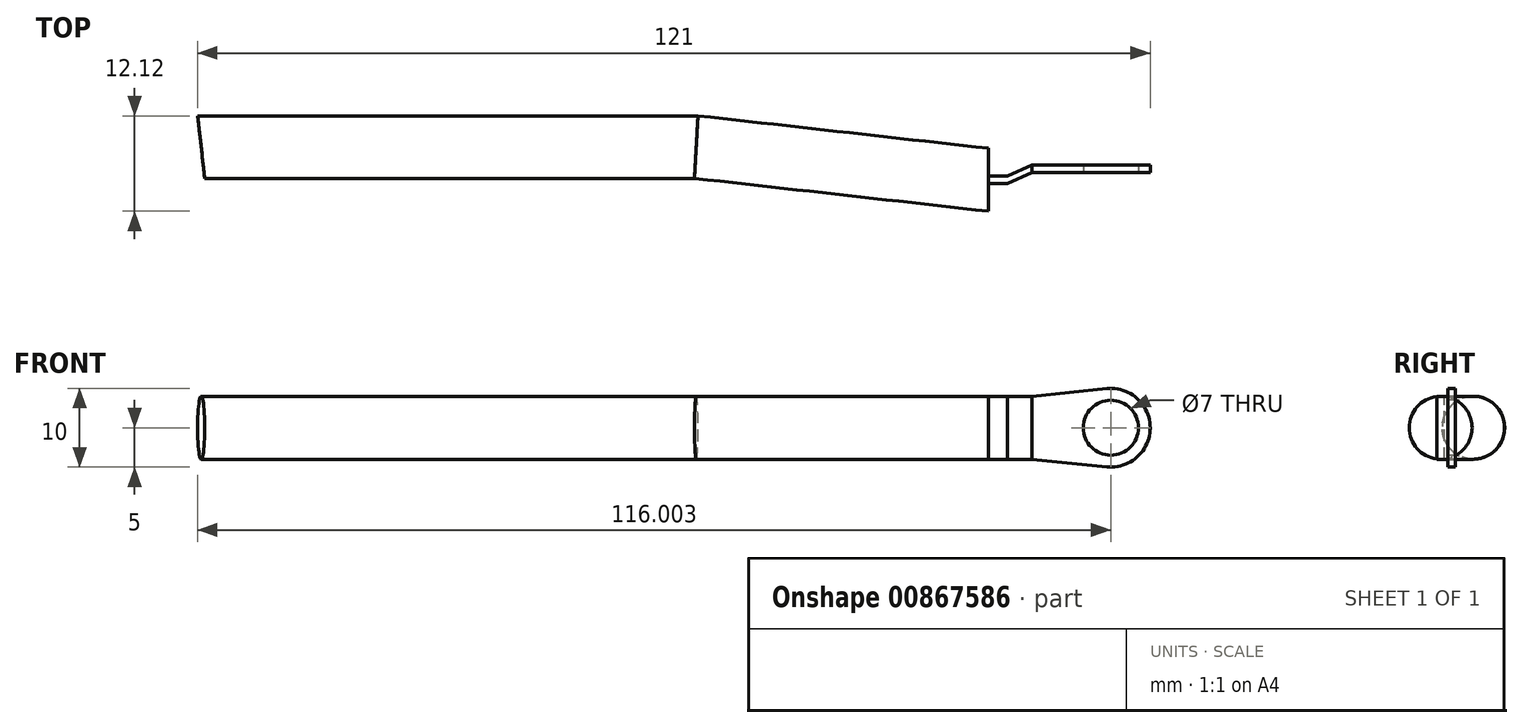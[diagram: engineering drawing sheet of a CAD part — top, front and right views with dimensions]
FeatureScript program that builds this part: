
annotation { "Feature Type Name" : "Feature", "Feature Type Description" : "" }
export const myFeature = defineFeature(function(context is Context, id is Id, definition is map)
    precondition{}
    {
        {
            var Q0;
            Q0=qCreatedBy(makeId("Front.planeOp"),FACE);
            var sketch = newSketch(context, id + "F0", { "sketchPlane" : qUnion([Q0])});
            skArc(sketch, "E0", {"start": v(12.63, -4.97) * mm, "mid": v(18.14, 0) * mm, "end": v(12.63, 4.97) * mm});
            skLineSegment(sketch, "E1", {"start": v(3.14, 4) * mm, "end": v(3.14, -4) * mm});
            skLineSegment(sketch, "E2", {"start": v(3.14, -4) * mm, "end": v(12.63, -4.97) * mm});
            skLineSegment(sketch, "E3", {"start": v(3.14, 4) * mm, "end": v(12.63, 4.97) * mm});
            skSolve(sketch);
        }
        {
            var Q0;
            Q0 = qSketchRegion(id + "F0", true);
            extrude(context, id + "F1", {"entities" : qUnion([Q0]), "endBound" : BoundingType.SYMMETRIC, "depth" : 1 * mm, "offsetDistance" : 25 * mm});
        }
        {
            var Q0;
            Q0=makeQuery(id+"F1.opExtrude","CAP_FACE",FACE,{"disambiguationData":[OSD([sQuery(id+"F0.wireOp",EDGE,"E0"),sQuery(id+"F0.wireOp",EDGE,"E1"),sQuery(id+"F0.wireOp",EDGE,"E2"),sQuery(id+"F0.wireOp",EDGE,"E3")])],"isStart":false});
            var sketch = newSketch(context, id + "F2", { "sketchPlane" : qUnion([Q0])});
            skCircle(sketch, "E4", {"center": v(13.14, 0) * mm, "radius": 3.5 * mm});
            skSolve(sketch);
        }
        {
            var Q0;
            Q0 = qSketchRegion(id + "F2", true);
            extrude(context, id + "F3", {"entities" : qUnion([Q0]), "operationType" : NewBodyOperationType.REMOVE, "oppositeDirection" : true, "depth" : 25 * mm, "offsetDistance" : 25 * mm});
        }
        {
            var Q0;
            Q0=qCreatedBy(makeId("Top.planeOp"),FACE);
            cPlane(context, id + "F4", {"entities" : qUnion([Q0]), "cplaneType" : CPlaneType.OFFSET, "offset" : 4 * mm, "flipAlignment" : true, "width" : 150 * mm, "height" : 150 * mm});
        }
        {
            var Q0;
            Q0=qCreatedBy(id+"F4.planeOp",FACE);
            var sketch = newSketch(context, id + "F5", { "sketchPlane" : qUnion([Q0])});
            skLineSegment(sketch, "E5", {"start": v(3.14, 0.5) * mm, "end": v(0, -0.9) * mm});
            skLineSegment(sketch, "E6", {"start": v(3.14, -0.5) * mm, "end": v(0, -1.9) * mm});
            skLineSegment(sketch, "E7", {"start": v(0, -0.9) * mm, "end": v(0, -1.9) * mm});
            skLineSegment(sketch, "E8", {"start": v(3.14, 0.5) * mm, "end": v(3.14, -0.5) * mm});
            skSolve(sketch);
        }
        {
            var Q0;
            Q0=qCreatedBy(id+"F4.planeOp",FACE);
            var sketch = newSketch(context, id + "F6", { "sketchPlane" : qUnion([Q0])});
            skLineSegment(sketch, "E9", {"start": v(0, -0.9) * mm, "end": v(-2.41, -0.9) * mm});
            skLineSegment(sketch, "E10", {"start": v(-2.41, -0.9) * mm, "end": v(-2.41, -1.9) * mm});
            skLineSegment(sketch, "E11", {"start": v(-2.41, -1.9) * mm, "end": v(0, -1.9) * mm});
            skLineSegment(sketch, "E12", {"start": v(0, -1.9) * mm, "end": v(0, -0.9) * mm});
            skSolve(sketch);
        }
        {
            var Q0;
            Q0 = qSketchRegion(id + "F5", true);
            var Q1;
            Q1 = qSketchRegion(id + "F6", true);
            extrude(context, id + "F7", {"entities" : qUnion([Q0, Q1]), "operationType" : NewBodyOperationType.ADD, "oppositeDirection" : true, "depth" : 8 * mm, "offsetDistance" : 25 * mm});
        }
        {
            var Q0;
            Q0=makeQuery(id+"F7.opExtrude","SWEPT_FACE",FACE,{"disambiguationData":[OSD([sQuery(id+"F6.wireOp",EDGE,"E10")])]});
            var sketch = newSketch(context, id + "F8", { "sketchPlane" : qUnion([Q0])});
            skCircle(sketch, "E13", {"center": v(1.4, 0) * mm, "radius": 4 * mm});
            skPoint(sketch, "E13.centerSnap0", {"position": v(1.9, 0) * mm});
            skPoint(sketch, "E13.centerSnap1", {"position": v(1.4, 4) * mm});
            skSolve(sketch);
        }
        {
            var Q0;
            {var subQ0=sQuery(id+"F8.wireOp",EDGE,"E13");var subQ1=sQuery(id+"F6.wireOp",EDGE,"E10");var subQ7=makeQuery(id+"F8.imprint","INTERSECT",VERTEX,{"derivedFrom":[makeQuery(id+"F7.opExtrude","CAP_EDGE",EDGE,{"disambiguationData":[OSD([subQ1])],"isStart":true}),subQ0]});Q0=makeQuery(id+"F8.imprint","IMPRINT",FACE,{"disambiguationData":[TD([[makeQuery(id+"F8.imprint","IMPRINT",EDGE,{"disambiguationData":[TD([[subQ7,1.0]])],"derivedFrom":subQ0}),1.0]])]});}
            cPlane(context, id + "F9", {"entities" : qUnion([Q0]), "cplaneType" : CPlaneType.OFFSET, "offset" : 100 * mm, "width" : 150 * mm, "height" : 150 * mm});
        }
        {
            var Q0;
            Q0=qCreatedBy(id+"F9.planeOp",FACE);
            var sketch = newSketch(context, id + "F10", { "sketchPlane" : qUnion([Q0])});
            skLineSegment(sketch, "E14", {"start": v(-7.74, 0) * mm, "end": v(8.6, 0) * mm, "construction": true});
            skCircle(sketch, "E15", {"center": v(-2.76, 0) * mm, "radius": 4 * mm});
            skSolve(sketch);
        }
        {
            var Q0;
            Q0=makeQuery(id+"F7.boolean.opBoolean","MERGE",FACE,{"derivedFrom":[makeQuery(id+"F7.opExtrude","CAP_FACE",FACE,{"disambiguationData":[OSD([sQuery(id+"F5.wireOp",EDGE,"E5"),sQuery(id+"F5.wireOp",EDGE,"E6"),sQuery(id+"F5.wireOp",EDGE,"E7"),sQuery(id+"F5.wireOp",EDGE,"E8")])],"isStart":true}),makeQuery(id+"F7.opExtrude","CAP_FACE",FACE,{"disambiguationData":[OSD([sQuery(id+"F6.wireOp",EDGE,"E9"),sQuery(id+"F6.wireOp",EDGE,"E10"),sQuery(id+"F6.wireOp",EDGE,"E11"),sQuery(id+"F6.wireOp",EDGE,"E12")])],"isStart":true})]});
            cPlane(context, id + "F11", {"entities" : qUnion([Q0]), "cplaneType" : CPlaneType.OFFSET, "offset" : 4 * mm, "oppositeDirection" : true, "width" : 150 * mm, "height" : 150 * mm});
        }
        {
            var Q0;
            Q0=qCreatedBy(id+"F11.planeOp",FACE);
            var sketch = newSketch(context, id + "F12", { "sketchPlane" : qUnion([Q0])});
            skLineSegment(sketch, "E16", {"start": v(-2.41, -1.4) * mm, "end": v(-39.53, 2.76) * mm});
            skLineSegment(sketch, "E17", {"start": v(-39.53, 2.76) * mm, "end": v(-102.41, 2.76) * mm});
            skSolve(sketch);
        }
        {
            var Q0;
            Q0 = qSketchRegion(id + "F8", true);
            var Q1;
            Q1=sQuery(id+"F12.wireOp",EDGE,"E16");
            var Q2;
            Q2=sQuery(id+"F12.wireOp",EDGE,"E17");
            sweep(context, id + "F13", {"profiles" : qUnion([Q0]), "path" : qUnion([Q1, Q2])});
        }
    });
